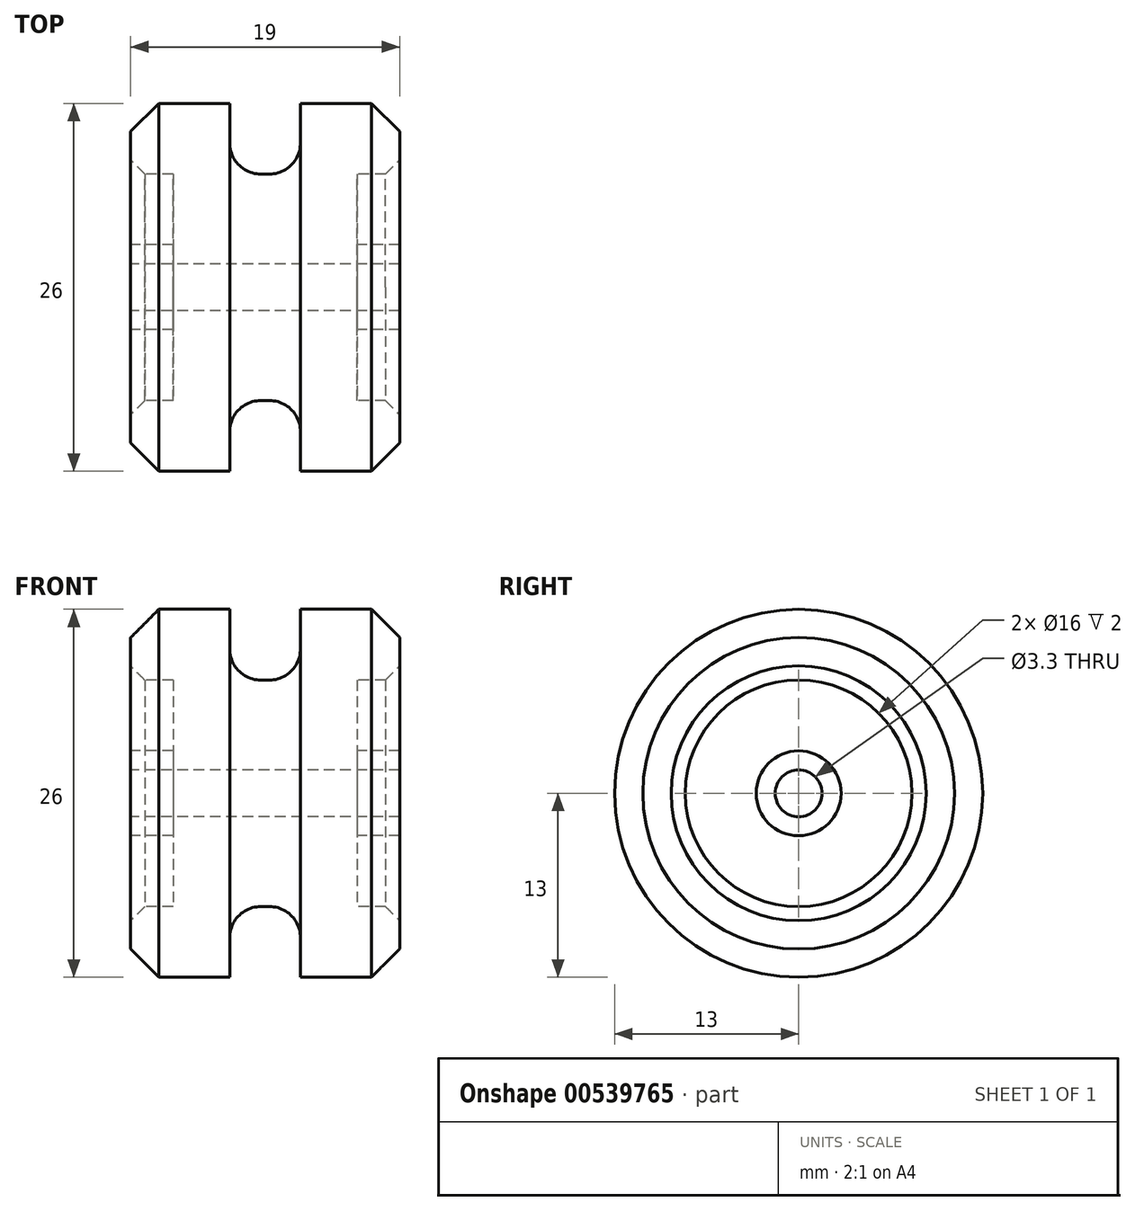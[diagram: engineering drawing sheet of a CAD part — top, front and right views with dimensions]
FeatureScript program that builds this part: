
annotation { "Feature Type Name" : "Feature", "Feature Type Description" : "" }
export const myFeature = defineFeature(function(context is Context, id is Id, definition is map)
    precondition{}
    {
        {
            var Q0;
            Q0=qCreatedBy(makeId("Top.planeOp"),FACE);
            var sketch = newSketch(context, id + "F0", { "sketchPlane" : qUnion([Q0])});
            skLineSegment(sketch, "E0", {"start": v(-20.04, 0) * mm, "end": v(-20.04, 3) * mm});
            skLineSegment(sketch, "E1", {"start": v(-20.04, 3) * mm, "end": v(-17.04, 3) * mm});
            skLineSegment(sketch, "E2", {"start": v(-17.04, 3) * mm, "end": v(-17.04, 8) * mm});
            skLineSegment(sketch, "E3", {"start": v(-17.04, 8) * mm, "end": v(-20.04, 8) * mm});
            skLineSegment(sketch, "E4", {"start": v(-20.04, 8) * mm, "end": v(-20.04, 13) * mm});
            skLineSegment(sketch, "E5", {"start": v(-20.04, 13) * mm, "end": v(-13.04, 13) * mm});
            skLineSegment(sketch, "E6", {"start": v(-13.04, 13) * mm, "end": v(-13.04, 8) * mm});
            skLineSegment(sketch, "E7", {"start": v(-13.04, 8) * mm, "end": v(-8.04, 8) * mm});
            skLineSegment(sketch, "E8", {"start": v(-8.04, 8) * mm, "end": v(-8.04, 13) * mm});
            skLineSegment(sketch, "E9", {"start": v(-8.04, 13) * mm, "end": v(-1.04, 13) * mm});
            skLineSegment(sketch, "E10", {"start": v(-1.04, 13) * mm, "end": v(-1.04, 8) * mm});
            skLineSegment(sketch, "E11", {"start": v(-1.04, 8) * mm, "end": v(-4.04, 8) * mm});
            skLineSegment(sketch, "E12", {"start": v(-4.04, 8) * mm, "end": v(-4.04, 3) * mm});
            skLineSegment(sketch, "E13", {"start": v(-4.04, 3) * mm, "end": v(-1.04, 3) * mm});
            skLineSegment(sketch, "E14", {"start": v(-1.04, 3) * mm, "end": v(-1.04, 0) * mm});
            skLineSegment(sketch, "E15", {"start": v(-1.04, 0) * mm, "end": v(-20.04, 0) * mm});
            skLineSegment(sketch, "E16", {"start": v(-21.37, 0) * mm, "end": v(0, 0) * mm, "construction": true});
            skSolve(sketch);
        }
        {
            var Q0;
            Q0=makeQuery(id+"F0.imprint","IMPRINT",FACE,{"disambiguationData":[TD([[makeQuery(id+"F0.imprint","IMPRINT",EDGE,{"derivedFrom":sQuery(id+"F0.wireOp",EDGE,"E0")}),-1.0]])]});
            var Q1;
            Q1=sQuery(id+"F0.wireOp",EDGE,"E16");
            revolve(context, id + "F1", {"entities" : qUnion([Q0]), "axis" : qUnion([Q1]), "revolveType" : RevolveType.FULL});
        }
        {
            var Q0;
            Q0=makeQuery(id+"F1.opRevolve","SWEPT_EDGE",EDGE,{"disambiguationData":[OSD([sQuery(id+"F0.wireOp",EDGE,"E10"),sQuery(id+"F0.wireOp",EDGE,"E11")])]});
            var Q1;
            Q1=makeQuery(id+"F1.opRevolve","SWEPT_EDGE",EDGE,{"disambiguationData":[OSD([sQuery(id+"F0.wireOp",EDGE,"E3"),sQuery(id+"F0.wireOp",EDGE,"E4")])]});
            chamfer(context, id + "F2", {"entities" : qUnion([Q0, Q1]), "width" : 1 * mm, "tangentPropagation" : true});
        }
        {
            var Q0;
            Q0=makeQuery(id+"F1.opRevolve","SWEPT_EDGE",EDGE,{"disambiguationData":[OSD([sQuery(id+"F0.wireOp",EDGE,"E4"),sQuery(id+"F0.wireOp",EDGE,"E5")])]});
            var Q1;
            Q1=makeQuery(id+"F1.opRevolve","SWEPT_EDGE",EDGE,{"disambiguationData":[OSD([sQuery(id+"F0.wireOp",EDGE,"E9"),sQuery(id+"F0.wireOp",EDGE,"E10")])]});
            chamfer(context, id + "F3", {"entities" : qUnion([Q0, Q1]), "width" : 2 * mm, "tangentPropagation" : true});
        }
        {
            var Q0;
            Q0=makeQuery(id+"F1.opRevolve","SWEPT_EDGE",EDGE,{"disambiguationData":[OSD([sQuery(id+"F0.wireOp",EDGE,"E6"),sQuery(id+"F0.wireOp",EDGE,"E7")])]});
            var Q1;
            Q1=makeQuery(id+"F1.opRevolve","SWEPT_EDGE",EDGE,{"disambiguationData":[OSD([sQuery(id+"F0.wireOp",EDGE,"E7"),sQuery(id+"F0.wireOp",EDGE,"E8")])]});
            fillet(context, id + "F4", {"entities" : qUnion([Q0, Q1]), "radius" : 2.2 * mm, "tangentPropagation" : true, "allowEdgeOverflow" : false});
        }
        {
            var Q0;
            Q0=makeQuery(id+"F1.opRevolve","SWEPT_FACE",FACE,{"disambiguationData":[OSD([sQuery(id+"F0.wireOp",EDGE,"E0")])]});
            var sketch = newSketch(context, id + "F5", { "sketchPlane" : qUnion([Q0])});
            skPoint(sketch, "E17", {"position": v(0, 0) * mm});
            skSolve(sketch);
        }
        {
            var Q0;
            Q0=sQuery(id+"F5.wireOp",VERTEX,"E17");
            var Q1;
            Q1=makeQuery(id+"F1.opRevolve","SWEPT_BODY",BODY,{"disambiguationData":[OSD([sQuery(id+"F0.wireOp",EDGE,"E0"),sQuery(id+"F0.wireOp",EDGE,"E1"),sQuery(id+"F0.wireOp",EDGE,"E2"),sQuery(id+"F0.wireOp",EDGE,"E3"),sQuery(id+"F0.wireOp",EDGE,"E4"),sQuery(id+"F0.wireOp",EDGE,"E5"),sQuery(id+"F0.wireOp",EDGE,"E6"),sQuery(id+"F0.wireOp",EDGE,"E7"),sQuery(id+"F0.wireOp",EDGE,"E8"),sQuery(id+"F0.wireOp",EDGE,"E9"),sQuery(id+"F0.wireOp",EDGE,"E10"),sQuery(id+"F0.wireOp",EDGE,"E11"),sQuery(id+"F0.wireOp",EDGE,"E12"),sQuery(id+"F0.wireOp",EDGE,"E13"),sQuery(id+"F0.wireOp",EDGE,"E14"),sQuery(id+"F0.wireOp",EDGE,"E15")])]});
            hole(context, id + "F6", {"style" : HoleStyle.SIMPLE, "endStyle" : HoleEndStyle.THROUGH, "holeDiameter" : 3.3 * mm, "isTappedThrough" : true, "tappedDepth" : 12 * mm, "tapClearance" : 3, "locations" : qUnion([Q0]), "scope" : qUnion([Q1])});
        }
    });
